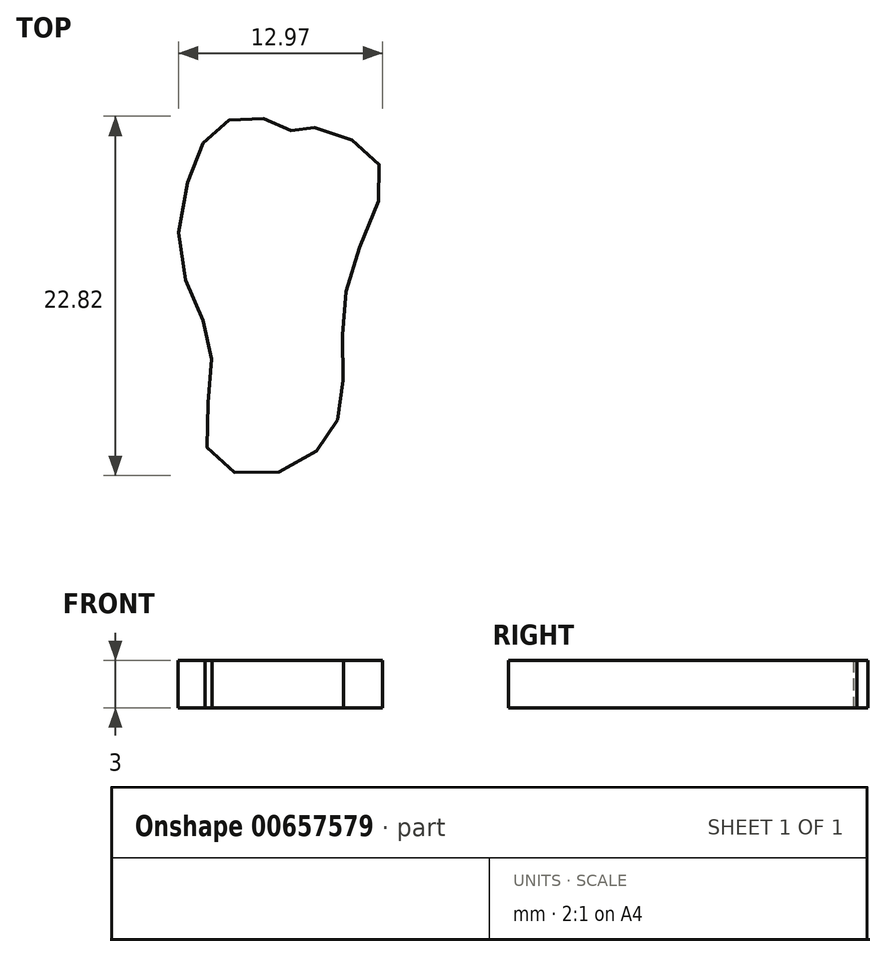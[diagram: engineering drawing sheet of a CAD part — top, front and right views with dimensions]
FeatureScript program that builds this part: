
annotation { "Feature Type Name" : "Feature", "Feature Type Description" : "" }
export const myFeature = defineFeature(function(context is Context, id is Id, definition is map)
    precondition{}
    {
        {
            var Q0;
            Q0=qCreatedBy(makeId("Top.planeOp"),FACE);
            var sketch = newSketch(context, id + "F0", { "sketchPlane" : qUnion([Q0])});
            skFitSpline(sketch, "E0", {"points": [v(-1.18, 15.18) * mm, v(-3.12, 16) * mm, v(-5.78, 15.49) * mm, v(-7.51, 12.62) * mm, v(-8.23, 7) * mm, v(-6.6, 2.7) * mm, v(-6.29, -1.07) * mm, v(-6.29, -5.47) * mm, v(-2.81, -6.7) * mm, v(0.87, -4.75) * mm, v(2.1, -1.79) * mm, v(2.1, 2.81) * mm, v(3.02, 7.3) * mm, v(4.65, 12.11) * mm, v(3.22, 14.26) * mm, v(0, 15.38) * mm, v(-1.18, 15.18) * mm]});
            skSolve(sketch);
        }
        {
            var Q0;
            Q0 = qSketchRegion(id + "F0", true);
            extrude(context, id + "F1", {"entities" : qUnion([Q0]), "depth" : 3 * mm, "offsetDistance" : 25 * mm});
        }
    });
